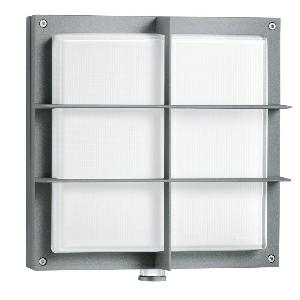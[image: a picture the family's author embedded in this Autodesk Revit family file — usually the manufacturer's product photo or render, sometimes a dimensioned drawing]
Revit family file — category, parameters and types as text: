
# Revit family: l_691_led_053031
name_source: partatom
category: Leuchten
revit_build: Autodesk Revit 2016 (Build: 20190508_0715(x64)
units: mm (PartAtom-declared; Revit-internal decimal feet)

## family parameters
Basisbauteil = Fläche
Beim Laden mit Abzugskörper schneiden = Nein
Bemaßung runder Anschluss = Durchmesser verwenden
Gemeinsam genutzt = Nein
Lichtquelle = Nein
Raumberechnungspunkt = Nein
Teiletyp = Normal

## types (1)
- L 691 LED (1 x , 753 lm, 3000 K)
    Beschreibung = Dimensions (L x W x H): 126 x 291 x 303 mm; Mains power supply: 220 – 240 V / 50 Hz; Mounting height max.: 2,50 m; Sensor Technology: passive infrared; Output: 9 W; Interconnection: Yes; Slave modeselectable: No; Luminous flux: 753 lm; Colour temperature: 3000 K; Colour variation LED: SDCM3; Colour Rendering Index CRI: 80-89; With lamp: Yes, STEINEL LED system; Lamp: LED cannot be replaced; LED life expectancy (max. °C): 50000 h; Base: without; LED cooling system: Passive Thermo Control; With motion detector: Yes; Detection angle: 360 °; Sneak-by guard: Yes; Capability of masking out individual segments: Yes; Electronic scalability: No; Mechanical scalability: No; Reach, radial: r = 1.5 m (7 m²); Reach, tangential: r = 7 m (154 m²); Photo-cell controller: Yes; Twilight setting: 2 – 1000 lx; Time setting: 5 sec – 15 min; Basic light level function: Yes; Basic light level function time: 10/30 min, all night; Functions: 4 programme settings geared to practical needs, can be selected on removable sensor module; Soft light start: Yes; Continuous light: selectable, 4h; Impact resistance: IK07; IP-rating: IP44; Protection class: II; Ambient temperature: -10 – 50 °C; Housing material: Aluminium; Cover material: Plastic, opal; Manufacturer's Warranty: 5 years; Settings via: Potentiometers; Cover material: shrouds; Version: PMMA anthracite; PU1, EAN: 4007841053031
    Color Rendering = 80-89
    Color Temperature = 3000 K
    Frequency = 50 Hz
    Height = 303 mm
    Hersteller = Steinel
    Lamp Light Flux = 753 lm
    Lamp count = 1
    Lampe = 1 x
    Length = 126 mm
    Luminous efficacy = 0 lm/W
    ModVariant = Nein
    Modell = 053031
    Mounting Type = Surface mounted
    Number of Poles = 1
    OnlyDefault = Ja
    Power Factor = 1
    Product Name = L 691 LED
    Product group = Sensor-switched indoor light
    ProductGroupID = 30
    Protection Class = Protection class II
    Protection Degree = IP 34
    RlxData = <blob elided: 62269 chars, md5=3906a3bf>
    Scheinlast = 9 VA
    Socket = socket
    Standby Power = 0 W
    System Light Flux = 0 lm
    System Power = 9 W
    Typenbild = produkt1_053031.jpg
    Typenkommentare = Product without accessories
    URL = http://relux.com
    VarID = ---
    Voltage = 0 V
    Vorgabe-Ansicht = 1800 mm
    Weight = 0.00 kg
    Width = 291 mm

## geometry (parser evidence)
native form markers: Blend x4, Sweep x11
no freeform markers — native parametric forms only
